# Revit family: Wavy Handle Type 1
name_source: partatom
category: Generic Models
units: mm (PartAtom-declared; Revit-internal decimal feet)

## family parameters
Always vertical = Yes
Can host rebar = No
Cut with Voids When Loaded = No
Host = Wall
Part Type = Normal
Room Calculation Point = No
Round Connector Dimension = Use Diameter
Shared = No

## types (4) — shared parameters
1 = 1 mm  [stored 0.00328084 ft]
2 = 2 mm  [stored 0.00656168 ft]
22 = 2 mm  [stored 0.00656168 ft]
222 = 2 mm  [stored 0.00656168 ft]
2222 = 2 mm  [stored 0.00656168 ft]
3 = 3 mm  [stored 0.00984252 ft]
4 = 4 mm  [stored 0.0131234 ft]
44 = 4 mm  [stored 0.0131234 ft]
444 = 3 mm  [stored 0.00984252 ft]
4444 = 4 mm  [stored 0.0131234 ft]
44444 = 3 mm  [stored 0.00984252 ft]
6 = 6 mm  [stored 0.019685 ft]
zero-valued in all types: Default Elevation

## per-type parameters (varying)
| type | Materials |
| Chiffon | Chiffon Glaze |
| Khaki | Khaki Glaze |
| Orange | Orange Glaze |
| Metallic Gold | Metallic Gold Glaze |

note: [stored X ft] marks values corroborated as IEEE doubles in the binary element streams (Revit-internal decimal feet)

## geometry (parser evidence)
native form markers: Sweep x2
no freeform markers — native parametric forms only
